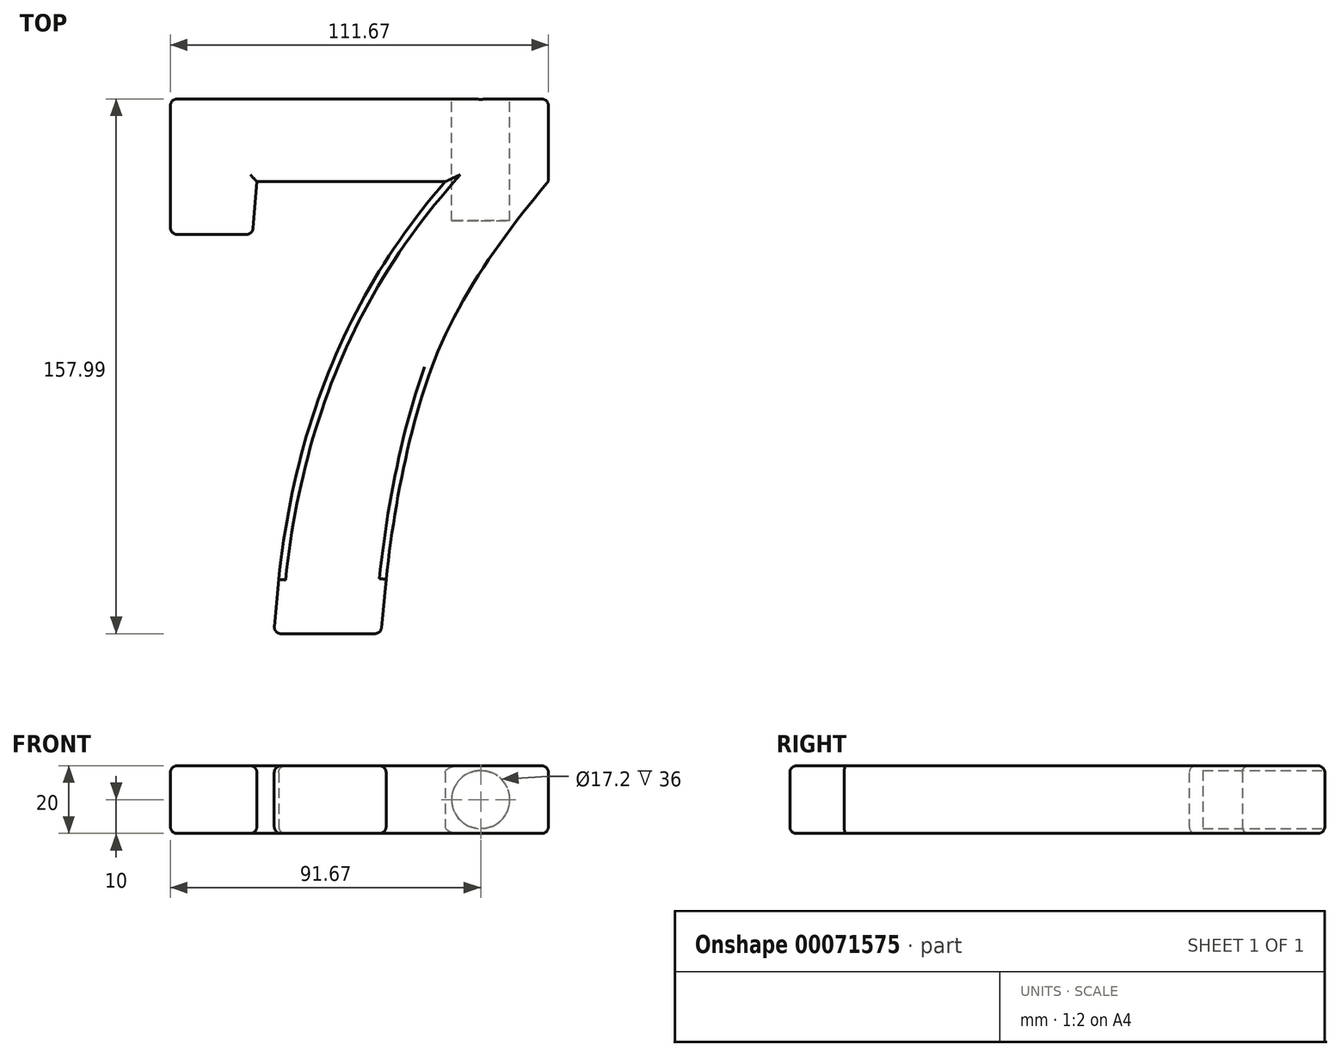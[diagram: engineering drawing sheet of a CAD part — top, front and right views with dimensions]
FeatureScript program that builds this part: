
annotation { "Feature Type Name" : "Feature", "Feature Type Description" : "" }
export const myFeature = defineFeature(function(context is Context, id is Id, definition is map)
    precondition{}
    {
        {
            var Q0;
            Q0=qCreatedBy(makeId("Top.planeOp"),FACE);
            var sketch = newSketch(context, id + "F0", { "sketchPlane" : qUnion([Q0])});
            skText(sketch, "E0", { "text": "7", "fontName": "RobotoSlab-Bold.ttf"});
            skLineSegment(sketch, "E1.bottom", {"start": v(29.99, 78) * mm, "end": v(46.99, 78) * mm, "construction": true});
            skLineSegment(sketch, "E1.top", {"start": v(29.99, 43) * mm, "end": v(46.99, 43) * mm, "construction": true});
            skLineSegment(sketch, "E1.left", {"start": v(29.99, 78) * mm, "end": v(29.99, 43) * mm, "construction": true});
            skLineSegment(sketch, "E1.right", {"start": v(46.99, 78) * mm, "end": v(46.99, 43) * mm, "construction": true});
            skPoint(sketch, "E2", {"position": v(-58.49, 0) * mm});
            const initialGuessF0  = {"E0": [-0.05849, -0.08, 1, 0, 0.16]};
            skSetInitialGuess(sketch, initialGuessF0);
            skSolve(sketch);
        }
        {
            var Q0;
            Q0=makeQuery(id+"F0.imprint","IMPRINT",FACE,{"disambiguationData":[TD([[makeQuery(id+"F0.imprint","IMPRINT",EDGE,{"derivedFrom":sQuery(id+"F0.wireOp",EDGE,"E0.sketch_text.stroke-0")}),-1.0]])]});
            extrude(context, id + "F1", {"entities" : qUnion([Q0]), "depth" : 20 * mm});
        }
        {
            var Q0;
            Q0=makeQuery(id+"F1.opExtrude","SWEPT_FACE",FACE,{"disambiguationData":[OSD([sQuery(id+"F0.wireOp",EDGE,"E0.sketch_text.stroke-11")])]});
            var sketch = newSketch(context, id + "F2", { "sketchPlane" : qUnion([Q0])});
            skLineSegment(sketch, "E3.0", {"start": v(-29.99, 0) * mm, "end": v(-46.99, 0) * mm, "construction": true});
            skPoint(sketch, "E4", {"position": v(-38.49, 0) * mm});
            skPoint(sketch, "E5", {"position": v(-38.49, 10) * mm});
            skPoint(sketch, "E5.positionSnap0", {"position": v(-58.49, 10) * mm});
            skCircle(sketch, "E6", {"center": v(-38.49, 10) * mm, "radius": 8.6 * mm});
            skSolve(sketch);
        }
        {
            var Q0;
            Q0=makeQuery(id+"F2.imprint","IMPRINT",FACE,{"disambiguationData":[TD([[makeQuery(id+"F2.imprint","IMPRINT",EDGE,{"derivedFrom":sQuery(id+"F2.wireOp",EDGE,"E6")}),1.0]])]});
            extrude(context, id + "F3", {"entities" : qUnion([Q0]), "operationType" : NewBodyOperationType.REMOVE, "oppositeDirection" : true, "depth" : 36 * mm});
        }
        {
            var Q0;
            Q0=makeQuery(id+"F1.opExtrude","CAP_EDGE",EDGE,{"disambiguationData":[OSD([sQuery(id+"F0.wireOp",EDGE,"E0.sketch_text.stroke-11")])],"isStart":false});
            var Q1;
            Q1=makeQuery(id+"F1.opExtrude","CAP_EDGE",EDGE,{"disambiguationData":[OSD([sQuery(id+"F0.wireOp",EDGE,"E0.sketch_text.stroke-11")])],"isStart":true});
            var Q2;
            Q2=makeQuery(id+"F1.opExtrude","SWEPT_EDGE",EDGE,{"disambiguationData":[OSD([sQuery(id+"F0.wireOp",EDGE,"E0.sketch_text.stroke-10"),sQuery(id+"F0.wireOp",EDGE,"E0.sketch_text.stroke-11")])]});
            var Q3;
            Q3=makeQuery(id+"F1.opExtrude","CAP_EDGE",EDGE,{"disambiguationData":[OSD([sQuery(id+"F0.wireOp",EDGE,"E0.sketch_text.stroke-9")])],"isStart":false});
            var Q4;
            Q4=makeQuery(id+"F1.opExtrude","CAP_EDGE",EDGE,{"disambiguationData":[OSD([sQuery(id+"F0.wireOp",EDGE,"E0.sketch_text.stroke-8")])],"isStart":false});
            var Q5;
            Q5=makeQuery(id+"F1.opExtrude","CAP_EDGE",EDGE,{"disambiguationData":[OSD([sQuery(id+"F0.wireOp",EDGE,"E0.sketch_text.stroke-7")])],"isStart":false});
            var Q6;
            Q6=makeQuery(id+"F1.opExtrude","CAP_EDGE",EDGE,{"disambiguationData":[OSD([sQuery(id+"F0.wireOp",EDGE,"E0.sketch_text.stroke-10")])],"isStart":false});
            var Q7;
            Q7=makeQuery(id+"F1.opExtrude","CAP_EDGE",EDGE,{"disambiguationData":[OSD([sQuery(id+"F0.wireOp",EDGE,"E0.sketch_text.stroke-10")])],"isStart":true});
            var Q8;
            Q8=makeQuery(id+"F1.opExtrude","SWEPT_EDGE",EDGE,{"disambiguationData":[OSD([sQuery(id+"F0.wireOp",EDGE,"E0.sketch_text.stroke-9"),sQuery(id+"F0.wireOp",EDGE,"E0.sketch_text.stroke-10")])]});
            var Q9;
            Q9=makeQuery(id+"F1.opExtrude","CAP_EDGE",EDGE,{"disambiguationData":[OSD([sQuery(id+"F0.wireOp",EDGE,"E0.sketch_text.stroke-12")])],"isStart":false});
            var Q10;
            Q10=makeQuery(id+"F1.opExtrude","SWEPT_EDGE",EDGE,{"disambiguationData":[OSD([sQuery(id+"F0.wireOp",EDGE,"E0.sketch_text.stroke-11"),sQuery(id+"F0.wireOp",EDGE,"E0.sketch_text.stroke-12")])]});
            var Q11;
            Q11=makeQuery(id+"F1.opExtrude","CAP_EDGE",EDGE,{"disambiguationData":[OSD([sQuery(id+"F0.wireOp",EDGE,"E0.sketch_text.stroke-12")])],"isStart":true});
            var Q12;
            Q12=makeQuery(id+"F1.opExtrude","CAP_EDGE",EDGE,{"disambiguationData":[OSD([sQuery(id+"F0.wireOp",EDGE,"E0.sketch_text.stroke-7")])],"isStart":true});
            var Q13;
            Q13=makeQuery(id+"F1.opExtrude","CAP_EDGE",EDGE,{"disambiguationData":[OSD([sQuery(id+"F0.wireOp",EDGE,"E0.sketch_text.stroke-8")])],"isStart":true});
            var Q14;
            Q14=makeQuery(id+"F1.opExtrude","CAP_EDGE",EDGE,{"disambiguationData":[OSD([sQuery(id+"F0.wireOp",EDGE,"E0.sketch_text.stroke-9")])],"isStart":true});
            var Q15;
            Q15=makeQuery(id+"F1.opExtrude","SWEPT_EDGE",EDGE,{"disambiguationData":[OSD([sQuery(id+"F0.wireOp",EDGE,"E0.sketch_text.stroke-8"),sQuery(id+"F0.wireOp",EDGE,"E0.sketch_text.stroke-9")])]});
            var Q16;
            Q16=makeQuery(id+"F1.opExtrude","CAP_EDGE",EDGE,{"disambiguationData":[OSD([sQuery(id+"F0.wireOp",EDGE,"E0.sketch_text.stroke-0")])],"isStart":false});
            var Q17;
            Q17=makeQuery(id+"F1.opExtrude","CAP_EDGE",EDGE,{"disambiguationData":[OSD([sQuery(id+"F0.wireOp",EDGE,"E0.sketch_text.stroke-1")])],"isStart":false});
            var Q18;
            Q18=makeQuery(id+"F1.opExtrude","SWEPT_EDGE",EDGE,{"disambiguationData":[OSD([sQuery(id+"F0.wireOp",EDGE,"E0.sketch_text.stroke-0"),sQuery(id+"F0.wireOp",EDGE,"E0.sketch_text.stroke-12")])]});
            var Q19;
            Q19=makeQuery(id+"F1.opExtrude","CAP_EDGE",EDGE,{"disambiguationData":[OSD([sQuery(id+"F0.wireOp",EDGE,"E0.sketch_text.stroke-0")])],"isStart":true});
            var Q20;
            Q20=makeQuery(id+"F1.opExtrude","CAP_EDGE",EDGE,{"disambiguationData":[OSD([sQuery(id+"F0.wireOp",EDGE,"E0.sketch_text.stroke-6")])],"isStart":false});
            var Q21;
            Q21=makeQuery(id+"F1.opExtrude","CAP_EDGE",EDGE,{"disambiguationData":[OSD([sQuery(id+"F0.wireOp",EDGE,"E0.sketch_text.stroke-6")])],"isStart":true});
            var Q22;
            Q22=makeQuery(id+"F1.opExtrude","SWEPT_EDGE",EDGE,{"disambiguationData":[OSD([sQuery(id+"F0.wireOp",EDGE,"E0.sketch_text.stroke-3"),sQuery(id+"F0.wireOp",EDGE,"E0.sketch_text.stroke-4")])]});
            var Q23;
            Q23=makeQuery(id+"F1.opExtrude","CAP_EDGE",EDGE,{"disambiguationData":[OSD([sQuery(id+"F0.wireOp",EDGE,"E0.sketch_text.stroke-3")])],"isStart":true});
            var Q24;
            Q24=makeQuery(id+"F1.opExtrude","SWEPT_EDGE",EDGE,{"disambiguationData":[OSD([sQuery(id+"F0.wireOp",EDGE,"E0.sketch_text.stroke-2"),sQuery(id+"F0.wireOp",EDGE,"E0.sketch_text.stroke-3")])]});
            var Q25;
            Q25=makeQuery(id+"F1.opExtrude","CAP_EDGE",EDGE,{"disambiguationData":[OSD([sQuery(id+"F0.wireOp",EDGE,"E0.sketch_text.stroke-3")])],"isStart":false});
            var Q26;
            Q26=makeQuery(id+"F1.opExtrude","CAP_EDGE",EDGE,{"disambiguationData":[OSD([sQuery(id+"F0.wireOp",EDGE,"E0.sketch_text.stroke-2")])],"isStart":true});
            var Q27;
            Q27=makeQuery(id+"F1.opExtrude","CAP_EDGE",EDGE,{"disambiguationData":[OSD([sQuery(id+"F0.wireOp",EDGE,"E0.sketch_text.stroke-2")])],"isStart":false});
            var Q28;
            Q28=makeQuery(id+"F1.opExtrude","CAP_EDGE",EDGE,{"disambiguationData":[OSD([sQuery(id+"F0.wireOp",EDGE,"E0.sketch_text.stroke-5")])],"isStart":false});
            var Q29;
            Q29=makeQuery(id+"F1.opExtrude","CAP_EDGE",EDGE,{"disambiguationData":[OSD([sQuery(id+"F0.wireOp",EDGE,"E0.sketch_text.stroke-4")])],"isStart":false});
            var Q30;
            Q30=makeQuery(id+"F1.opExtrude","CAP_EDGE",EDGE,{"disambiguationData":[OSD([sQuery(id+"F0.wireOp",EDGE,"E0.sketch_text.stroke-5")])],"isStart":true});
            var Q31;
            Q31=makeQuery(id+"F1.opExtrude","CAP_EDGE",EDGE,{"disambiguationData":[OSD([sQuery(id+"F0.wireOp",EDGE,"E0.sketch_text.stroke-4")])],"isStart":true});
            var Q32;
            Q32=makeQuery(id+"F1.opExtrude","CAP_EDGE",EDGE,{"disambiguationData":[OSD([sQuery(id+"F0.wireOp",EDGE,"E0.sketch_text.stroke-1")])],"isStart":true});
            fillet(context, id + "F4", {"entities" : qUnion([Q0, Q1, Q2, Q3, Q4, Q5, Q6, Q7, Q8, Q9, Q10, Q11, Q12, Q13, Q14, Q15, Q16, Q17, Q18, Q19, Q20, Q21, Q22, Q23, Q24, Q25, Q26, Q27, Q28, Q29, Q30, Q31, Q32]), "radius" : 2 * mm, "tangentPropagation" : true, "allowEdgeOverflow" : false});
        }
    });
